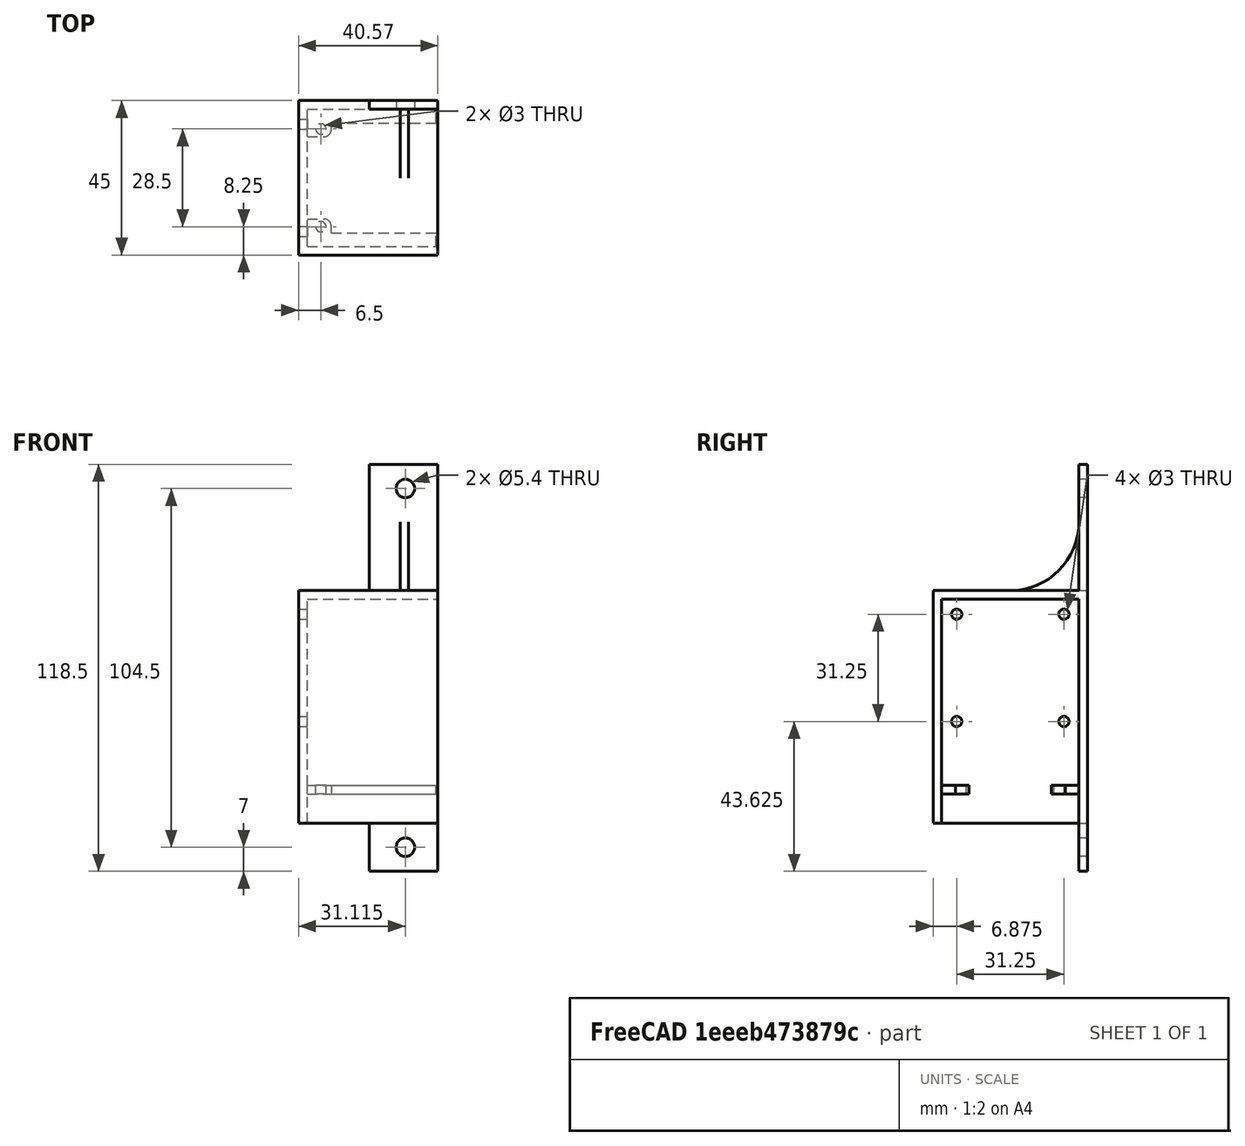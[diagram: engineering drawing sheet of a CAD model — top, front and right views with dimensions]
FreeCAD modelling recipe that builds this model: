
FCSTD DOCUMENT  (FreeCAD 0.16R6706 (Git))
Label: S2H-head-box
License: All rights reserved
LicenseURL: http://en.wikipedia.org/wiki/All_rights_reserved
objects: Part::Cut×11, Part::Cylinder×8, Part::Box×7, Part::Thickness×1, Part::MultiFuse×1, Part::Fillet×1
note: 29 computed .brp shape members not serialized (recipe doc carries the construction recipe); baked Part::Feature solids carry a one-line shape summary decoded from their .brp

FEATURE [Part::Box] Box  label="box base template"
  Height = 67.75
  Length = 40.57
  Width = 45
FEATURE [Part::Thickness] Thickness
  Faces = -> Box [Face2,Face5]
  Intersection = false
  Join = 0
  Mode = 0
  SelfIntersection = false
  Value = -2.5
FEATURE [Part::Box] Box001  label="Cube001"
  Height = 2.5
  Length = 37.5
  Placement = pos=(2.5,2.5,8.5) rot=(0,0,1;0rad)
  Width = 8
FEATURE [Part::Box] Box004  label="Cube004"
  Height = 2.5
  Length = 37.5
  Placement = pos=(2.5,34.5,8.5) rot=(0,0,1;0rad)
  Width = 8
FEATURE [Part::Cylinder] Cylinder
  Angle = 360
  Height = 2.5
  Placement = pos=(10.545,2.5,-7) rot=(1,0,0;1.5708rad)
  Radius = 2.7
FEATURE [Part::Box] Box007  label="Cube007"
  Height = 14
  Length = 20
  Placement = pos=(0,0,-14) rot=(0,0,1;0rad)
  Width = 2.5
FEATURE [Part::Cut] Cut  label="tab1"
  Base = -> Box007
  Placement = pos=(20.57,42.5,0) rot=(0,0,1;0rad)
  Tool = -> Cylinder
FEATURE [Part::Cylinder] Cylinder002
  Angle = 360
  Height = 2.5
  Placement = pos=(10.545,2.5,-7) rot=(1,0,0;1.5708rad)
  Radius = 2.7
FEATURE [Part::Box] Box009  label="Cube009"
  Height = 36.75
  Length = 20
  Placement = pos=(0,0,-36.75) rot=(0,0,1;0rad)
  Width = 2.5
FEATURE [Part::Cut] Cut002  label="tab2"
  Base = -> Box009
  Placement = pos=(20.57,42.5,104.5) rot=(0,0,1;0rad)
  Tool = -> Cylinder002
FEATURE [Part::Cylinder] Cylinder003
  Angle = 360
  Height = 2.5
  Placement = pos=(0,38.125,29.625) rot=(0,1,0;1.5708rad)
  Radius = 1.5
FEATURE [Part::Cylinder] Cylinder004
  Angle = 360
  Height = 2.5
  Placement = pos=(0,6.875,29.625) rot=(0,1,0;1.5708rad)
  Radius = 1.5
FEATURE [Part::Cylinder] Cylinder005
  Angle = 360
  Height = 2.5
  Placement = pos=(0,38.125,60.875) rot=(0,1,0;1.5708rad)
  Radius = 1.5
FEATURE [Part::Cylinder] Cylinder006
  Angle = 360
  Height = 2.5
  Placement = pos=(0,6.875,60.875) rot=(0,1,0;1.5708rad)
  Radius = 1.5
FEATURE [Part::Box] Box010  label="Cube"
  Height = 20
  Length = 2.5
  Placement = pos=(29.57,22.5,67.75) rot=(0,0,1;0rad)
  Width = 20
FEATURE [Part::Cylinder] Cylinder007
  Angle = 360
  Height = 2.5
  Placement = pos=(29.57,22.5,87.75) rot=(0,1,0;1.5708rad)
  Radius = 20
FEATURE [Part::Cut] Cut007  label="wedge"
  Base = -> Box010
  Tool = -> Cylinder007
FEATURE [Part::Cut] Cut008
  Base = -> Box001
FEATURE [Part::Cut] Cut010
  Base = -> Thickness
  Tool = -> Cylinder006
FEATURE [Part::Cut] Cut011
  Base = -> Cut010
  Tool = -> Cylinder005
FEATURE [Part::Cut] Cut012
  Base = -> Cut011
  Tool = -> Cylinder004
FEATURE [Part::Cut] Cut013  label="base2"
  Base = -> Cut012
  Tool = -> Cylinder003
FEATURE [Part::Cylinder] Cylinder009
  Angle = 360
  Height = 10
  Placement = pos=(6.5,36.75,8.5) rot=(0,0,1;0rad)
  Radius = 1.5
FEATURE [Part::Cut] Cut014
  Base = -> Box004
  Tool = -> Cylinder009
FEATURE [Part::Box] Box011  label="Cube010"
  Height = 2.5
  Length = 31
  Placement = pos=(9.5,6.5,8.5) rot=(0,0,1;0rad)
  Width = 32
FEATURE [Part::Cut] Cut015
  Base = -> Cut008
  Tool = -> Box011
FEATURE [Part::Cut] Cut016
  Base = -> Cut014
  Tool = -> Box011
FEATURE [Part::MultiFuse] Fusion
  Shapes = -> [Cut013,Cut007,Cut002,Cut,Cut015,Cut016]
FEATURE [Part::Fillet] Fillet
  Base = -> Fusion
  Edges = 2 edges r=2: [Edge104,Edge110]
